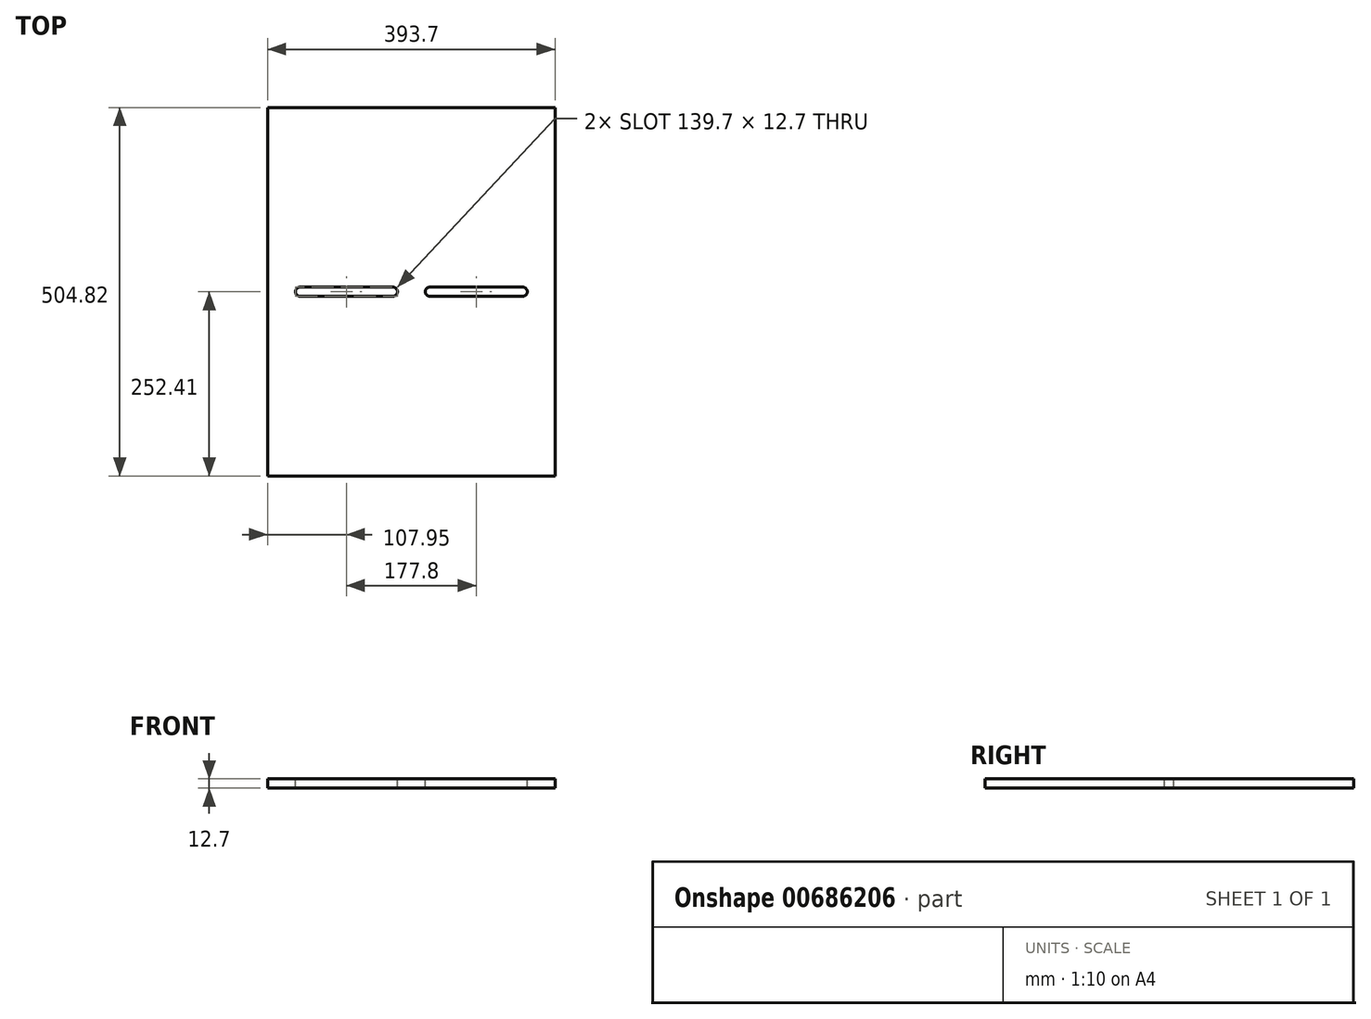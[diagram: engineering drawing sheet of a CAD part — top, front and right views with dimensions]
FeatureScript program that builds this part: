
annotation { "Feature Type Name" : "Feature", "Feature Type Description" : "" }
export const myFeature = defineFeature(function(context is Context, id is Id, definition is map)
    precondition{}
    {
        {
            var Q0;
            Q0=qCreatedBy(makeId("Top.planeOp"),FACE);
            var sketch = newSketch(context, id + "F0", { "sketchPlane" : qUnion([Q0])});
            skLineSegment(sketch, "E0.bottom", {"start": v(-196.85, 252.41) * mm, "end": v(196.85, 252.41) * mm});
            skLineSegment(sketch, "E0.top", {"start": v(-196.85, -252.41) * mm, "end": v(196.85, -252.41) * mm});
            skLineSegment(sketch, "E0.left", {"start": v(-196.85, 252.41) * mm, "end": v(-196.85, -252.41) * mm});
            skLineSegment(sketch, "E0.right", {"start": v(196.85, 252.41) * mm, "end": v(196.85, -252.41) * mm});
            skPoint(sketch, "E0.middle", {"position": v(0, 0) * mm});
            skSolve(sketch);
        }
        {
            var Q0;
            Q0 = qSketchRegion(id + "F0", true);
            extrude(context, id + "F1", {"entities" : qUnion([Q0]), "depth" : 12.7 * mm, "offsetDistance" : 25.4 * mm});
        }
        {
            var Q0;
            Q0=qCreatedBy(makeId("Top.planeOp"),FACE);
            var sketch = newSketch(context, id + "F2", { "sketchPlane" : qUnion([Q0])});
            skLineSegment(sketch, "E1", {"start": v(-152.4, 0) * mm, "end": v(-25.4, 0) * mm});
            skLineSegment(sketch, "E2", {"start": v(0, 70.53) * mm, "end": v(0, -100.76) * mm, "construction": true});
            skLineSegment(sketch, "E3.MirrorCS", {"start": v(152.4, 0) * mm, "end": v(25.4, 0) * mm});
            skArc(sketch, "E4.0.startCap", {"start": v(-152.4, -6.35) * mm, "mid": v(-158.75, 0) * mm, "end": v(-152.4, 6.35) * mm});
            skArc(sketch, "E4.0.endCap", {"start": v(-25.4, 6.35) * mm, "mid": v(-19.05, 0) * mm, "end": v(-25.4, -6.35) * mm});
            skLineSegment(sketch, "E4.0.left", {"start": v(-152.4, 6.35) * mm, "end": v(-25.4, 6.35) * mm});
            skLineSegment(sketch, "E4.0.right", {"start": v(-152.4, -6.35) * mm, "end": v(-25.4, -6.35) * mm});
            skArc(sketch, "E4.1.startCap", {"start": v(152.4, 6.35) * mm, "mid": v(158.75, 0) * mm, "end": v(152.4, -6.35) * mm});
            skArc(sketch, "E4.1.endCap", {"start": v(25.4, -6.35) * mm, "mid": v(19.05, 0) * mm, "end": v(25.4, 6.35) * mm});
            skLineSegment(sketch, "E4.1.left", {"start": v(152.4, -6.35) * mm, "end": v(25.4, -6.35) * mm});
            skLineSegment(sketch, "E4.1.right", {"start": v(152.4, 6.35) * mm, "end": v(25.4, 6.35) * mm});
            skSolve(sketch);
        }
        {
            var Q0;
            Q0 = qSketchRegion(id + "F2", true);
            extrude(context, id + "F3", {"entities" : qUnion([Q0]), "operationType" : NewBodyOperationType.REMOVE, "endBound" : BoundingType.SYMMETRIC, "oppositeDirection" : true, "depth" : 25.4 * mm, "offsetDistance" : 25.4 * mm});
        }
    });
